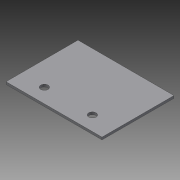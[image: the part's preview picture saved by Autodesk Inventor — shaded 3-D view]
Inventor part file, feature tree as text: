
AUTODESK INVENTOR PART (.ipt)
format: ipt  version: 2015 (Build 190159000, 159)  size: 93,696 bytes
history: native  units: mm
features: extrude x3, sketch x3, other x1
ambient origin geometry x8: Origin, YZ Plane, XZ Plane, XY Plane, X Axis, Y Axis, Z Axis, Center Point
bodies: Body1 (feature_tree)
feature tree (7):
  other  "ソリッド1"
  extrude  "押し出し1"  Depth=40.0mm
  extrude  "押し出し2"  Depth=40.0mm
  extrude  "押し出し3"  Depth=1.0mm TaperAngle=0.0deg
  sketch  "スケッチ1"
  sketch  "スケッチ2"
  sketch  "スケッチ3"
